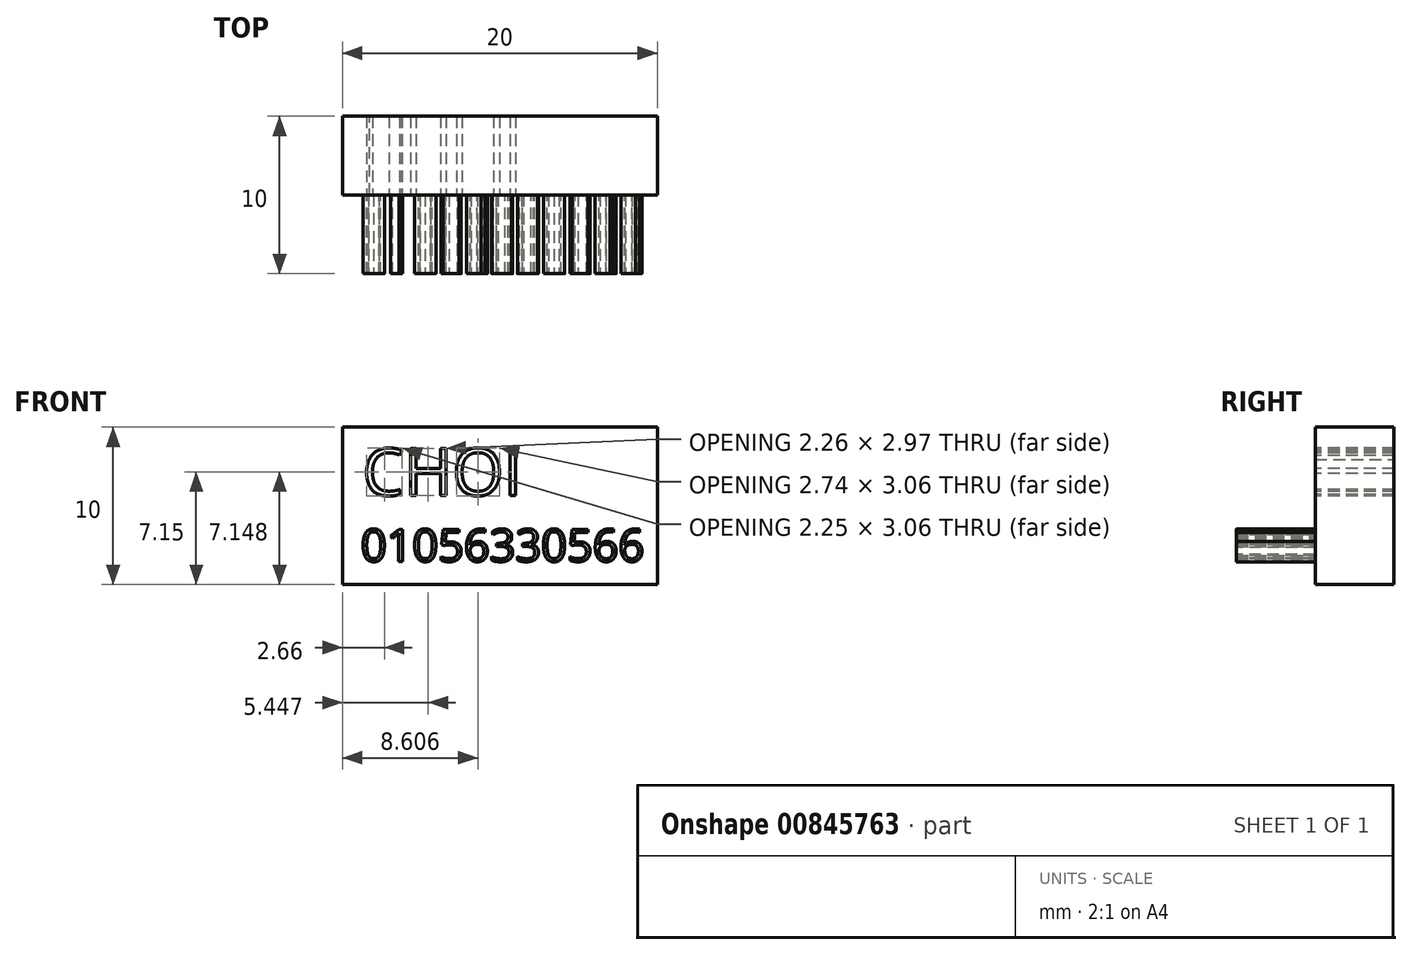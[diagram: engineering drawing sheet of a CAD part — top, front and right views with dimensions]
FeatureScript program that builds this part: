
annotation { "Feature Type Name" : "Feature", "Feature Type Description" : "" }
export const myFeature = defineFeature(function(context is Context, id is Id, definition is map)
    precondition{}
    {
        {
            var Q0;
            Q0=qCreatedBy(makeId("Front.planeOp"),FACE);
            var sketch = newSketch(context, id + "F0", { "sketchPlane" : qUnion([Q0])});
            skLineSegment(sketch, "E0.bottom", {"start": v(0, 0) * mm, "end": v(20, 0) * mm});
            skLineSegment(sketch, "E0.top", {"start": v(0, 10) * mm, "end": v(20, 10) * mm});
            skLineSegment(sketch, "E0.left", {"start": v(0, 0) * mm, "end": v(0, 10) * mm});
            skLineSegment(sketch, "E0.right", {"start": v(20, 0) * mm, "end": v(20, 10) * mm});
            skSolve(sketch);
        }
        {
            var Q0;
            Q0=makeQuery(id+"F0.imprint","IMPRINT",FACE,{"disambiguationData":[TD([[makeQuery(id+"F0.imprint","IMPRINT",EDGE,{"derivedFrom":sQuery(id+"F0.wireOp",EDGE,"E0.bottom")}),1.0]])]});
            extrude(context, id + "F1", {"entities" : qUnion([Q0]), "depth" : 5 * mm, "offsetDistance" : 25 * mm});
        }
        {
            var Q0;
            Q0=makeQuery(id+"F1.opExtrude","CAP_FACE",FACE,{"disambiguationData":[OSD([sQuery(id+"F0.wireOp",EDGE,"E0.bottom"),sQuery(id+"F0.wireOp",EDGE,"E0.top"),sQuery(id+"F0.wireOp",EDGE,"E0.left"),sQuery(id+"F0.wireOp",EDGE,"E0.right")])],"isStart":false});
            var sketch = newSketch(context, id + "F2", { "sketchPlane" : qUnion([Q0])});
            skText(sketch, "E1", { "text": "CHOI\n", "fontName": "OpenSans-Regular.ttf"});
            const initialGuessF2  = {"E1": [0.00128, 0.00566, 1, 0, 0.003]};
            skSetInitialGuess(sketch, initialGuessF2);
            skSolve(sketch);
        }
        {
            var Q0;
            Q0 = qSketchRegion(id + "F2", true);
            extrude(context, id + "F3", {"entities" : qUnion([Q0]), "operationType" : NewBodyOperationType.REMOVE, "oppositeDirection" : true, "depth" : 25 * mm, "offsetDistance" : 25 * mm});
        }
        {
            var Q0;
            {var subQ0=sQuery(id+"F0.wireOp",EDGE,"E0.top");var subQ1=sQuery(id+"F0.wireOp",EDGE,"E0.right");var subQ2=sQuery(id+"F0.wireOp",EDGE,"E0.bottom");var subQ3=sQuery(id+"F0.wireOp",EDGE,"E0.left");Q0=makeQuery(id+"F3.boolean.opBoolean","SPLIT",FACE,{"disambiguationData":[TD([makeQuery(id+"F1.opExtrude","SWEPT_FACE",FACE,{"disambiguationData":[OSD([subQ2])]})])],"derivedFrom":makeQuery(id+"F1.opExtrude","CAP_FACE",FACE,{"disambiguationData":[OSD([subQ2,subQ0,subQ3,subQ1])],"isStart":false})});}
            var sketch = newSketch(context, id + "F4", { "sketchPlane" : qUnion([Q0])});
            skText(sketch, "E2", { "text": "01056330566", "fontName": "OpenSans-Regular.ttf"});
            const initialGuessF4  = {"E2": [0.00117, 0.00147, 1, 0, 0.00206]};
            skSetInitialGuess(sketch, initialGuessF4);
            skSolve(sketch);
        }
        {
            var Q0;
            Q0 = qSketchRegion(id + "F4", true);
            extrude(context, id + "F5", {"entities" : qUnion([Q0]), "operationType" : NewBodyOperationType.ADD, "depth" : 5 * mm, "offsetDistance" : 25 * mm});
        }
    });
